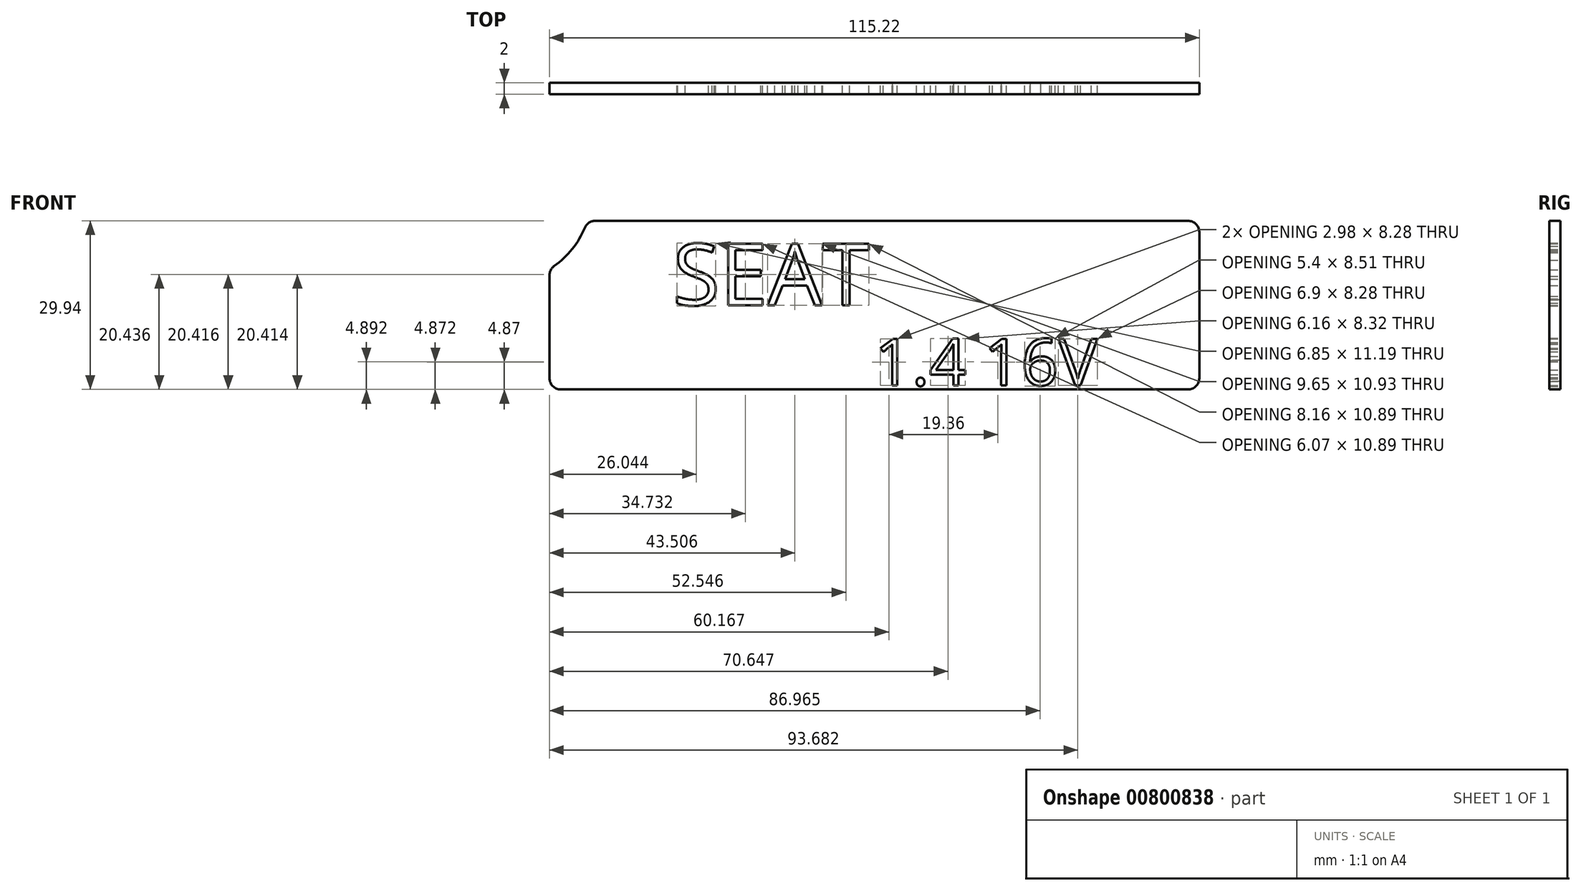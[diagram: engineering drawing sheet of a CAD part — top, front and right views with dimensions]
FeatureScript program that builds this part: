
annotation { "Feature Type Name" : "Feature", "Feature Type Description" : "" }
export const myFeature = defineFeature(function(context is Context, id is Id, definition is map)
    precondition{}
    {
        {
            var Q0;
            Q0=qCreatedBy(makeId("Front.planeOp"),FACE);
            var sketch = newSketch(context, id + "F0", { "sketchPlane" : qUnion([Q0])});
            skLineSegment(sketch, "E0.bottom", {"start": v(-55.61, 14.97) * mm, "end": v(55.61, 14.97) * mm});
            skLineSegment(sketch, "E0.top", {"start": v(-55.61, -14.97) * mm, "end": v(55.61, -14.97) * mm});
            skLineSegment(sketch, "E0.left", {"start": v(-57.61, 12.97) * mm, "end": v(-57.61, -12.97) * mm});
            skLineSegment(sketch, "E0.right", {"start": v(57.61, 12.97) * mm, "end": v(57.61, -12.97) * mm});
            skPoint(sketch, "E0.middle", {"position": v(0, 0) * mm});
            skPoint(sketch, "E1.visualSharp", {"position": v(-57.61, -14.97) * mm});
            skArc(sketch, "E1.filletArc", {"start": v(-57.61, -12.97) * mm, "mid": v(-57.03, -14.38) * mm, "end": v(-55.61, -14.97) * mm});
            skPoint(sketch, "E2.visualSharp", {"position": v(57.61, -14.97) * mm});
            skArc(sketch, "E2.filletArc", {"start": v(55.61, -14.97) * mm, "mid": v(57.03, -14.38) * mm, "end": v(57.61, -12.97) * mm});
            skPoint(sketch, "E3.visualSharp", {"position": v(57.61, 14.97) * mm});
            skArc(sketch, "E3.filletArc", {"start": v(57.61, 12.97) * mm, "mid": v(57.03, 14.38) * mm, "end": v(55.61, 14.97) * mm});
            skCircle(sketch, "E4", {"center": v(-65.96, 19.87) * mm, "radius": 15.84 * mm});
            skPoint(sketch, "E5.visualSharp", {"position": v(-57.61, 14.97) * mm});
            skArc(sketch, "E5.filletArc", {"start": v(-55.61, 14.97) * mm, "mid": v(-57.03, 14.38) * mm, "end": v(-57.61, 12.97) * mm});
            skSolve(sketch);
        }
        {
            var Q0;
            Q0=makeQuery(id+"F0.imprint","IMPRINT",FACE,{"disambiguationData":[TD([[makeQuery(id+"F0.imprint","IMPRINT",EDGE,{"derivedFrom":sQuery(id+"F0.wireOp",EDGE,"E0.top")}),1.0]])]});
            extrude(context, id + "F1", {"entities" : qUnion([Q0]), "depth" : 2 * mm, "offsetDistance" : 25 * mm});
        }
        {
            var Q0;
            Q0=makeQuery(id+"F1.opExtrude","SWEPT_EDGE",EDGE,{"disambiguationData":[OSD([sQuery(id+"F0.wireOp",EDGE,"E0.left"),sQuery(id+"F0.wireOp",EDGE,"E4")])]});
            var Q1;
            Q1=makeQuery(id+"F1.opExtrude","SWEPT_EDGE",EDGE,{"disambiguationData":[OSD([sQuery(id+"F0.wireOp",EDGE,"E0.bottom"),sQuery(id+"F0.wireOp",EDGE,"E4")])]});
            fillet(context, id + "F2", {"entities" : qUnion([Q0, Q1]), "radius" : 2 * mm, "tangentPropagation" : true, "allowEdgeOverflow" : false});
        }
        {
            var Q0;
            Q0=qCreatedBy(makeId("Front.planeOp"),FACE);
            var sketch = newSketch(context, id + "F3", { "sketchPlane" : qUnion([Q0])});
            skText(sketch, "E6", { "text": "SEAT", "fontName": "OpenSans-Regular.ttf"});
            const initialGuessF3  = {"E6": [-0.03578, 0, 1, 0, 0.01098]};
            skSetInitialGuess(sketch, initialGuessF3);
            skSolve(sketch);
        }
        {
            var Q0;
            Q0 = qSketchRegion(id + "F3", true);
            extrude(context, id + "F4", {"entities" : qUnion([Q0]), "operationType" : NewBodyOperationType.REMOVE, "depth" : 20.3 * mm, "offsetDistance" : 25 * mm});
        }
        {
            var Q0;
            Q0=qCreatedBy(makeId("Front.planeOp"),FACE);
            var sketch = newSketch(context, id + "F5", { "sketchPlane" : qUnion([Q0])});
            skText(sketch, "E7", { "text": "1.4 16V", "fontName": "OpenSans-Regular.ttf"});
            const initialGuessF5  = {"E7": [0, -0.01424, 1, 0, 0.00835]};
            skSetInitialGuess(sketch, initialGuessF5);
            skSolve(sketch);
        }
        {
            var Q0;
            Q0 = qSketchRegion(id + "F5", true);
            extrude(context, id + "F6", {"entities" : qUnion([Q0]), "operationType" : NewBodyOperationType.REMOVE, "depth" : 15.8 * mm, "offsetDistance" : 25 * mm});
        }
    });
